# Revit family: 918f47cc-9ef0-47f9-9d96-2d76202690ad
name_source: partatom
category: Plumbing Fixtures
revit_build: Autodesk Revit 2014 (Build: 20130308_1515(x64)
units: mm (PartAtom-declared; Revit-internal decimal feet)

## types (1)
- 918f47cc-9ef0-47f9-9d96-2d76202690ad
    Assembly Code = D2010110
    Default Elevation = 0' - 0"
    Electrical_Frequency = 60 Hz
    Electrical_Voltage = 120 V
    Electrical_Wattage = 1300 W
    Expected Lifespan (Years) = 0
    Fixture Finish = Finish - TOTO - Cotton 01
    GPF = 1
    GPF Dual = 0.8
    Keynote = 22 40 00
    Maintenance Schedule (Months) = 0
    Manufacturer = TOTO USA
    Manufacturer Fax = 770-282-8697
    Manufacturer Website = http://www.totousa.com
    Model = As Specified
    Product Data = http://www.arcat.com
    Revision = R1_2016-12
    Sales Information = http://www.totousa.com
    Seat Height = 0' - 0"
    Standards Conformance = as Specified
    Trap Seal = 0' - 2 1/16"
    URL = http://www.totousa.com
    Unit Depth = 2' - 7 7/16"
    Unit Height = 1' - 8 3/4"
    Unit Weight = 123.6
    Unit Width = 1' - 5 5/8"
    Warranty Duration (Years) = 0

## geometry (parser evidence)
native form markers: Sweep x3
no freeform markers — native parametric forms only
